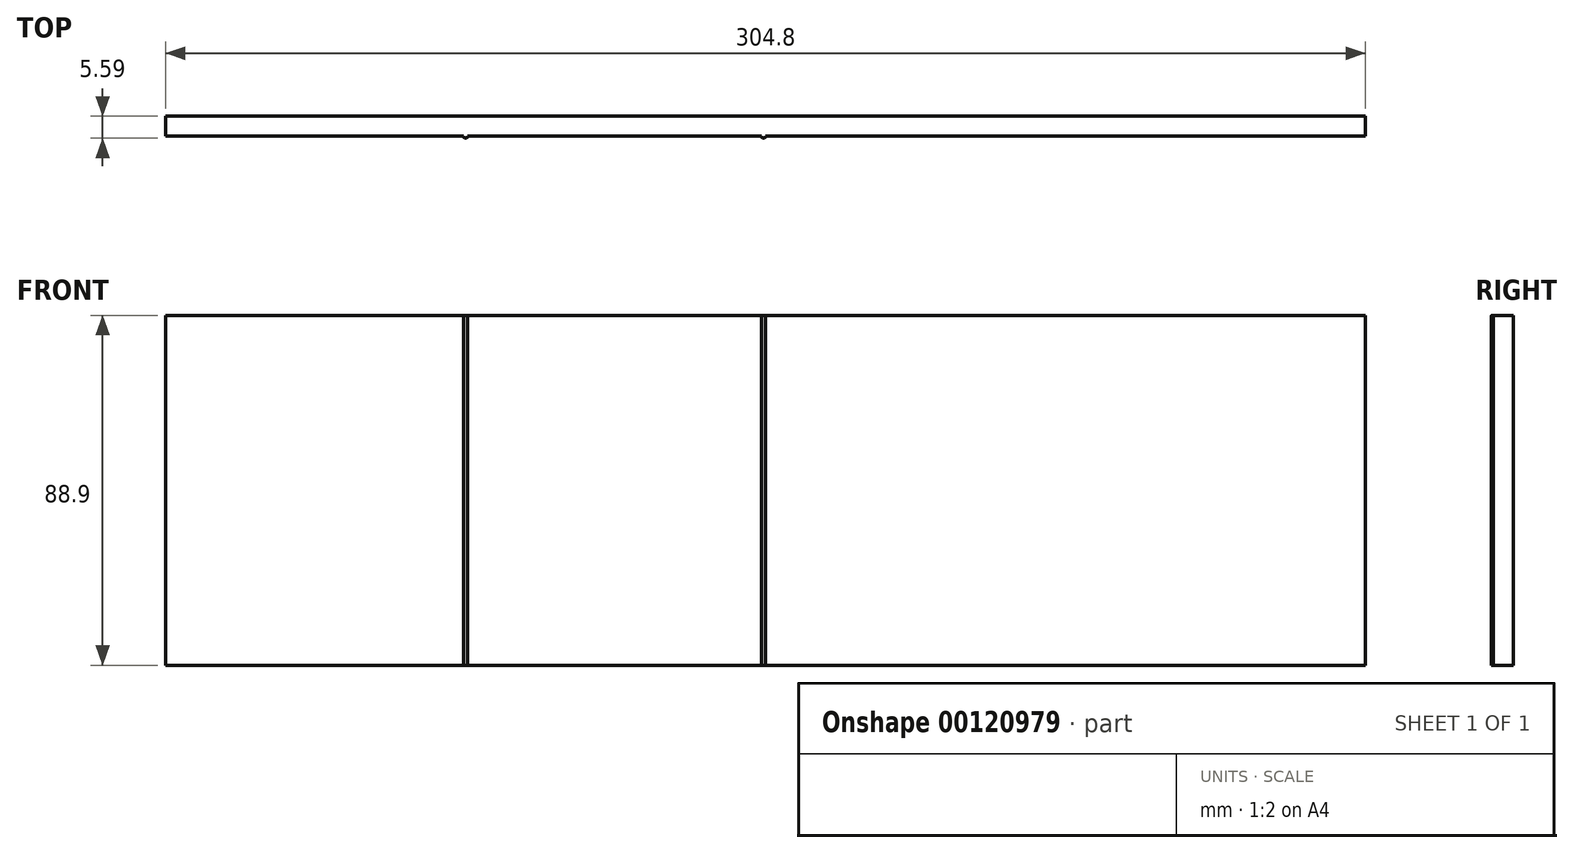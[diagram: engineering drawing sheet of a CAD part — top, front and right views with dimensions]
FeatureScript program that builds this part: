
annotation { "Feature Type Name" : "Feature", "Feature Type Description" : "" }
export const myFeature = defineFeature(function(context is Context, id is Id, definition is map)
    precondition{}
    {
        {
            var Q0;
            Q0=qCreatedBy(makeId("Front.planeOp"),FACE);
            var sketch = newSketch(context, id + "F0", { "sketchPlane" : qUnion([Q0])});
            skLineSegment(sketch, "E0.bottom", {"start": v(-110.02, 20.94) * mm, "end": v(194.78, 20.94) * mm});
            skLineSegment(sketch, "E0.top", {"start": v(-110.02, -67.96) * mm, "end": v(194.78, -67.96) * mm});
            skLineSegment(sketch, "E0.left", {"start": v(-110.02, 20.94) * mm, "end": v(-110.02, -67.96) * mm});
            skLineSegment(sketch, "E0.right", {"start": v(194.78, 20.94) * mm, "end": v(194.78, -67.96) * mm});
            skLineSegment(sketch, "E1", {"start": v(-33.82, 20.94) * mm, "end": v(-33.82, -67.96) * mm});
            skLineSegment(sketch, "E2", {"start": v(42.38, 20.94) * mm, "end": v(42.38, -67.96) * mm});
            skLineSegment(sketch, "E3.0", {"start": v(-33.31, 20.94) * mm, "end": v(-33.31, -67.96) * mm});
            skLineSegment(sketch, "E4.0", {"start": v(41.87, 20.94) * mm, "end": v(41.87, -67.96) * mm});
            skSolve(sketch);
        }
        {
            var Q0;
            Q0=qSketchRegion(id+"F0",true);
            extrude(context, id + "F1", {"entities" : qUnion([Q0]), "oppositeDirection" : true, "depth" : 5.08 * mm});
        }
        {
            var Q0;
            {var subQ0=sQuery(id+"F0.wireOp",EDGE,"E1");Q0=makeQuery(id+"F0.imprint","IMPRINT",FACE,{"disambiguationData":[TD([[makeQuery(id+"F0.imprint","IMPRINT",EDGE,{"derivedFrom":subQ0}),1.0]])]});}
            var Q1;
            Q1=sQuery(id+"F0.wireOp",EDGE,"E1");
            revolve(context, id + "F2", {"operationType" : NewBodyOperationType.ADD, "entities" : qUnion([Q0]), "axis" : qUnion([Q1]), "revolveType" : RevolveType.FULL});
        }
        {
            var Q0;
            {var subQ0=sQuery(id+"F0.wireOp",EDGE,"E2");Q0=makeQuery(id+"F0.imprint","IMPRINT",FACE,{"disambiguationData":[TD([[makeQuery(id+"F0.imprint","IMPRINT",EDGE,{"derivedFrom":subQ0}),-1.0]])]});}
            var Q1;
            Q1=sQuery(id+"F0.wireOp",EDGE,"E4.0");
            revolve(context, id + "F3", {"operationType" : NewBodyOperationType.ADD, "entities" : qUnion([Q0]), "axis" : qUnion([Q1]), "revolveType" : RevolveType.FULL});
        }
    });
